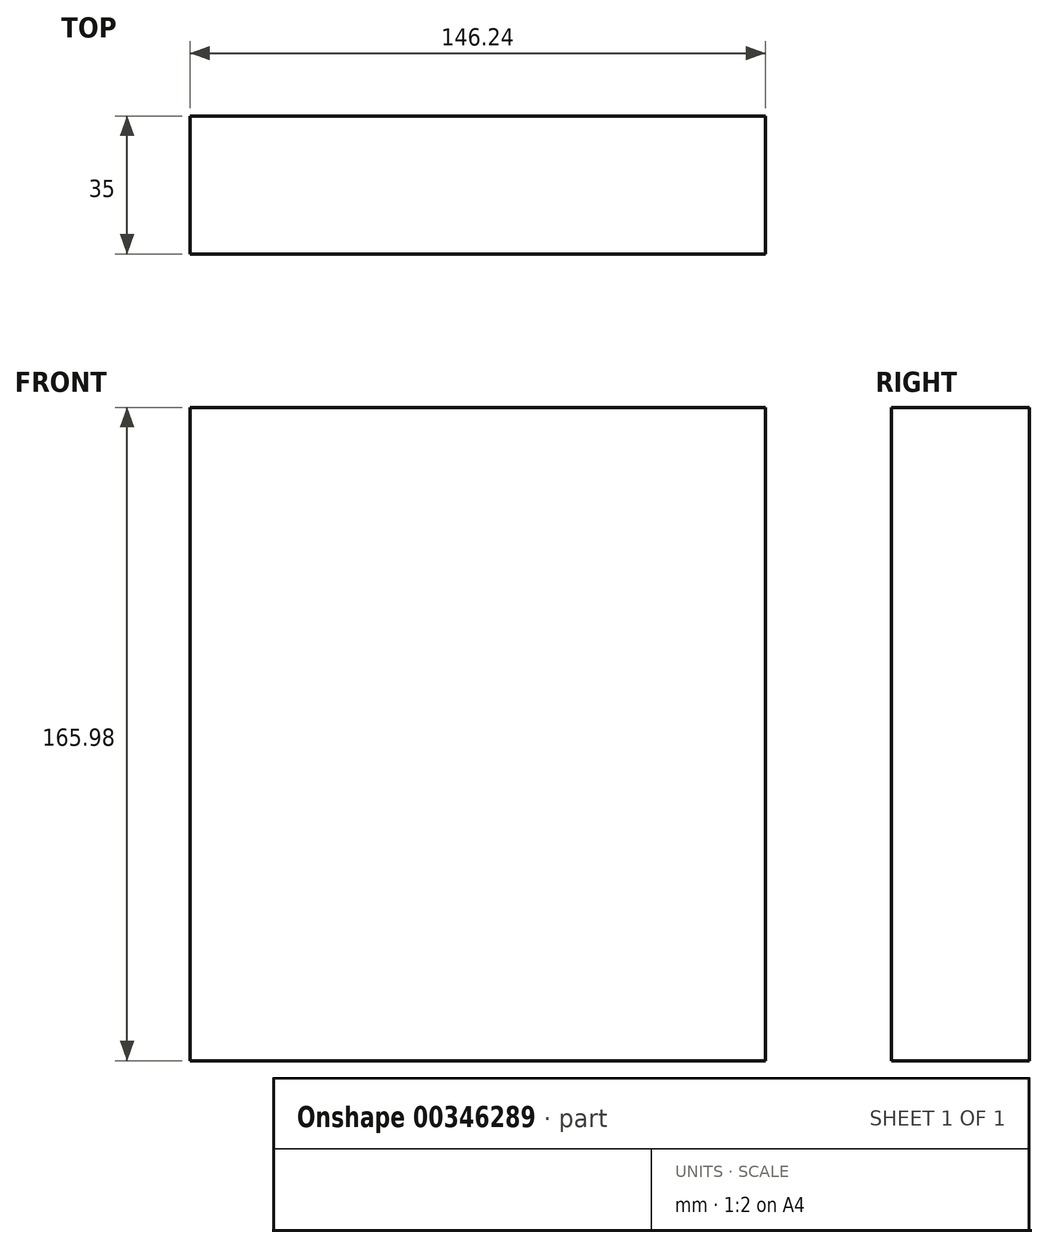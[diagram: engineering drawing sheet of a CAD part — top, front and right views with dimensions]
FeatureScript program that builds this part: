
annotation { "Feature Type Name" : "Feature", "Feature Type Description" : "" }
export const myFeature = defineFeature(function(context is Context, id is Id, definition is map)
    precondition{}
    {
        {
            var Q0;
            Q0=qCreatedBy(makeId("Front.planeOp"),FACE);
            var sketch = newSketch(context, id + "F0", { "sketchPlane" : qUnion([Q0])});
            skLineSegment(sketch, "E0.bottom", {"start": v(-85.62, 83) * mm, "end": v(85.62, 83) * mm});
            skLineSegment(sketch, "E0.top", {"start": v(-85.62, -83) * mm, "end": v(85.62, -83) * mm});
            skLineSegment(sketch, "E0.left", {"start": v(-85.62, 83) * mm, "end": v(-85.62, -83) * mm});
            skLineSegment(sketch, "E0.right", {"start": v(85.62, 83) * mm, "end": v(85.62, -83) * mm});
            skPoint(sketch, "E0.middle", {"position": v(0, 0) * mm});
            skSolve(sketch);
        }
        {
            var Q0;
            Q0=makeQuery(id+"F0.imprint","IMPRINT",FACE,{"disambiguationData":[TD([[makeQuery(id+"F0.imprint","IMPRINT",EDGE,{"derivedFrom":sQuery(id+"F0.wireOp",EDGE,"E0.bottom")}),-1.0]])]});
            extrude(context, id + "F1", {"entities" : qUnion([Q0]), "oppositeDirection" : true, "depth" : 35 * mm});
        }
        {
            var Q0;
            Q0=makeQuery(id+"F1.opExtrude","SWEPT_FACE",FACE,{"disambiguationData":[OSD([sQuery(id+"F0.wireOp",EDGE,"E0.right")])]});
            extrude(context, id + "F2", {"entities" : qUnion([Q0]), "operationType" : NewBodyOperationType.REMOVE, "oppositeDirection" : true, "depth" : 25 * mm});
        }
    });
